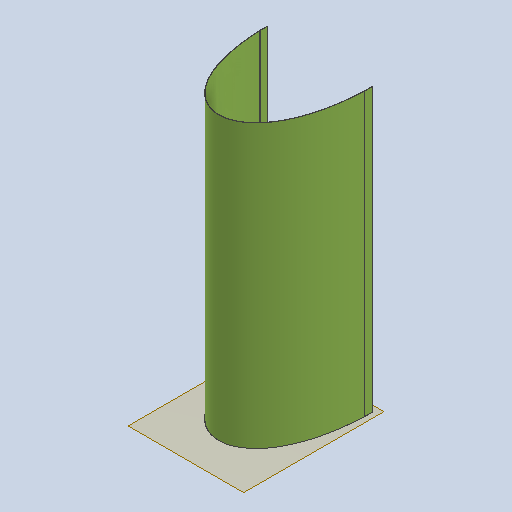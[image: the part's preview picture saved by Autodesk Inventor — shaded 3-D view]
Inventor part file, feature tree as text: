
AUTODESK INVENTOR PART (.ipt)
format: ipt  version: 2023 (Build 270158030, 158C)  size: 117,760 bytes
history: native  units: mm
features: other x3, plane x2, reference x2, sketch x1, extrude x1
ambient origin geometry x8: Origin, YZ Plane, XZ Plane, XY Plane, X Axis, Y Axis, Z Axis, Center Point
bodies: Body1 (feature_tree)
feature tree (9):
  other  "cover-deployed"
  plane  "Work Plane1"
  sketch  "Sketch1"  dims[d0=2.0mm d1=10.0mm d2=0.0mm]
  plane  "Work Plane2"
  extrude  "Extrusion1"  Depth=10.0mm TaperAngle=0.0deg
  reference  "Reference1"
  reference  "Reference2"
  other  "primary-engineer-bench.iam"
  other  "back-flaps-3:2"
